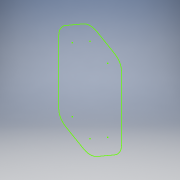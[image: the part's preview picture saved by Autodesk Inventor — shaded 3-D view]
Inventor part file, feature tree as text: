
AUTODESK INVENTOR PART (.ipt)
format: ipt  version: 2018 (Build 220112000, 112)  size: 87,040 bytes
history: native  units: in
note: dims shown in document units (in); Inventor stores cm internally (conversion verified against a paired STEP export)
features: sketch x1
ambient origin geometry x8: Origin, YZ Plane, XZ Plane, XY Plane, X Axis, Y Axis, Z Axis, Center Point
feature tree (1):
  sketch  "Sketch1"
